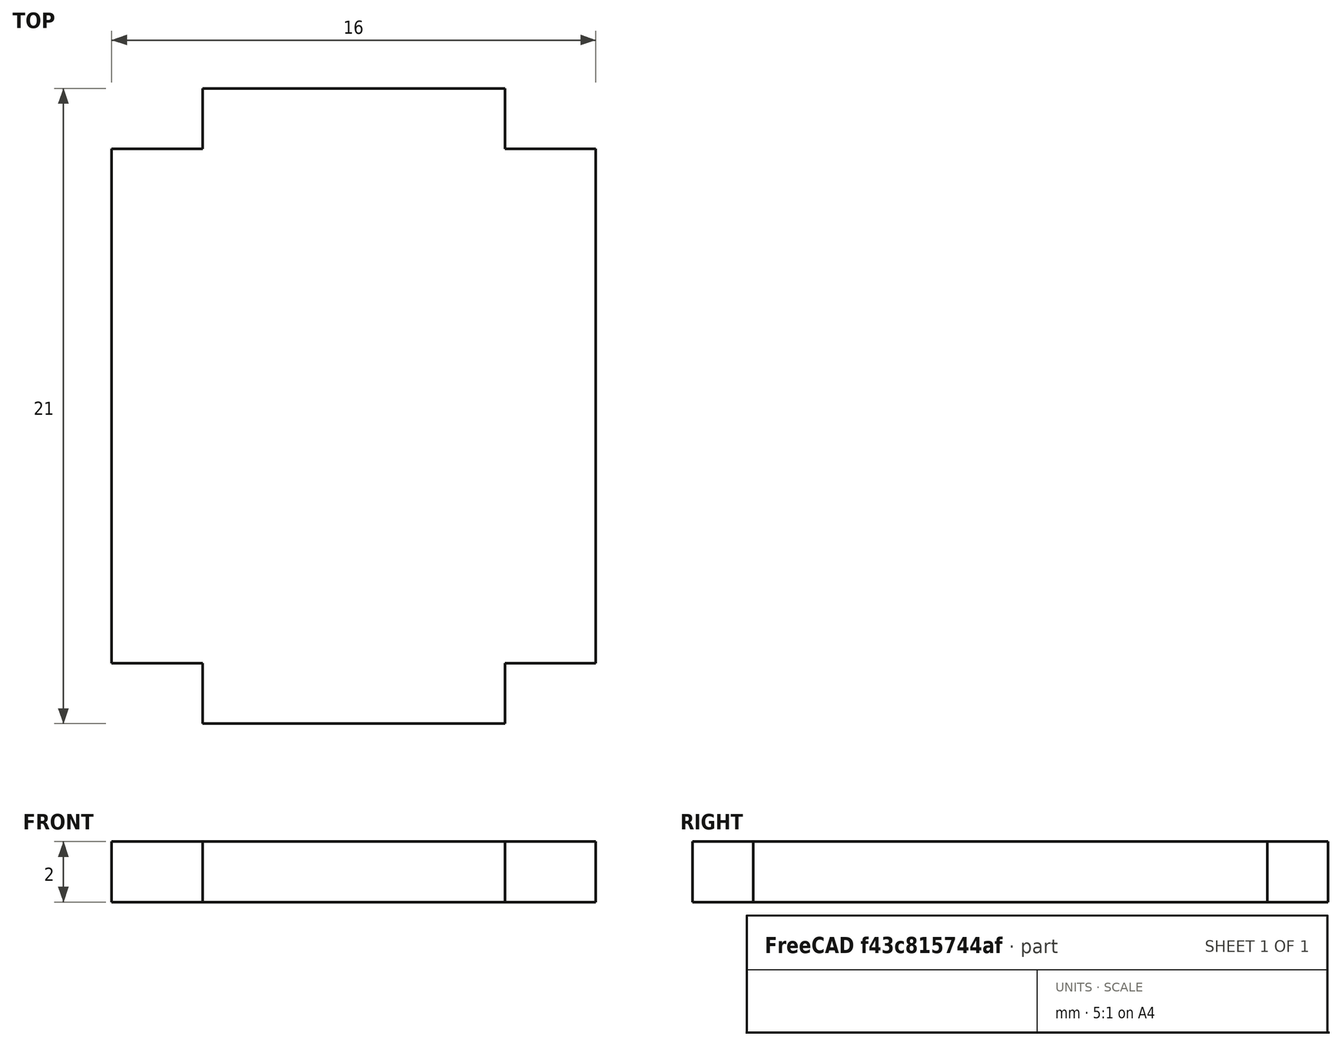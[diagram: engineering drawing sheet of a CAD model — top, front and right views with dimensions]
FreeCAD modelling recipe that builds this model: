
FCSTD DOCUMENT  (FreeCAD 0.18R16131 (Git))
Label: tibia_H_haut
License: All rights reserved
LicenseURL: http://en.wikipedia.org/wiki/All_rights_reserved
objects: Sketcher::SketchObject×1, PartDesign::Pad×1, PartDesign::Body×1
note: 4 computed .brp shape members not serialized (recipe doc carries the construction recipe); baked Part::Feature solids carry a one-line shape summary decoded from their .brp

FEATURE [Sketcher::SketchObject] Sketch
  MapMode = 5
  Support = -> [XY_Plane]
  sketch-geometry (12):
    g0: LineSegment StartX=0 StartY=19 StartZ=0 EndX=0 EndY=2 EndZ=0
    g1: LineSegment StartX=0 StartY=2 StartZ=0 EndX=3 EndY=2 EndZ=0
    g2: LineSegment StartX=3 StartY=2 StartZ=0 EndX=3 EndY=0 EndZ=0
    g3: LineSegment StartX=3 StartY=0 StartZ=0 EndX=13 EndY=0 EndZ=0
    g4: LineSegment StartX=13 StartY=0 StartZ=0 EndX=13 EndY=2 EndZ=0
    g5: LineSegment StartX=13 StartY=2 StartZ=0 EndX=16 EndY=2 EndZ=0
    g6: LineSegment StartX=16 StartY=2 StartZ=0 EndX=16 EndY=19 EndZ=0
    g7: LineSegment StartX=16 StartY=19 StartZ=0 EndX=13 EndY=19 EndZ=0
    g8: LineSegment StartX=13 StartY=19 StartZ=0 EndX=13 EndY=21 EndZ=0
    g9: LineSegment StartX=13 StartY=21 StartZ=0 EndX=3 EndY=21 EndZ=0
    g10: LineSegment StartX=3 StartY=21 StartZ=0 EndX=3 EndY=19 EndZ=0
    g11: LineSegment StartX=3 StartY=19 StartZ=0 EndX=0 EndY=19 EndZ=0
  constraints (36):
    c: Coincident(g0,g1)
    c: Coincident(g1,g2)
    c: Coincident(g2,g3)
    c: Coincident(g3,g4)
    c: Coincident(g4,g5)
    c: Coincident(g5,g6)
    c: Coincident(g6,g7)
    c: Coincident(g7,g8)
    c: Coincident(g8,g9)
    c: Coincident(g9,g10)
    c: Coincident(g10,g11)
    c: Coincident(g11,g0)
    c: Vertical(g0)
    c: Vertical(g10)
    c: Vertical(g8)
    c: Vertical(g6)
    c: Vertical(g4)
    c: Vertical(g2)
    c: Horizontal(g11)
    c: Horizontal(g9)
    c: Horizontal(g7)
    c: Horizontal(g5)
    c: Horizontal(g1)
    c: Horizontal(g3)
    c: PointOnObject(g2,g-1)
    c: PointOnObject(g0,g-2)
    c: Equal(g4,g2)
    c: Equal(g2,g10)
    c: Equal(g10,g8)
    c: DistanceY(g8,g8) = 2
    c: Vertical(g10,g2)
    c: DistanceY(g0,g0) = 17
    c: Equal(g3,g9)
    c: DistanceX(g9,g9) = 10
    c: DistanceX(g0,g5) = 16
    c: DistanceX(g1,g1) = 3
FEATURE [PartDesign::Pad] Pad
  Length = 2
  Length2 = 100
  Profile = -> Sketch
  Type = 0
FEATURE [PartDesign::Body] Body
  Group = -> [Sketch,Pad]
  Origin = -> Origin
  Tip = -> Pad
